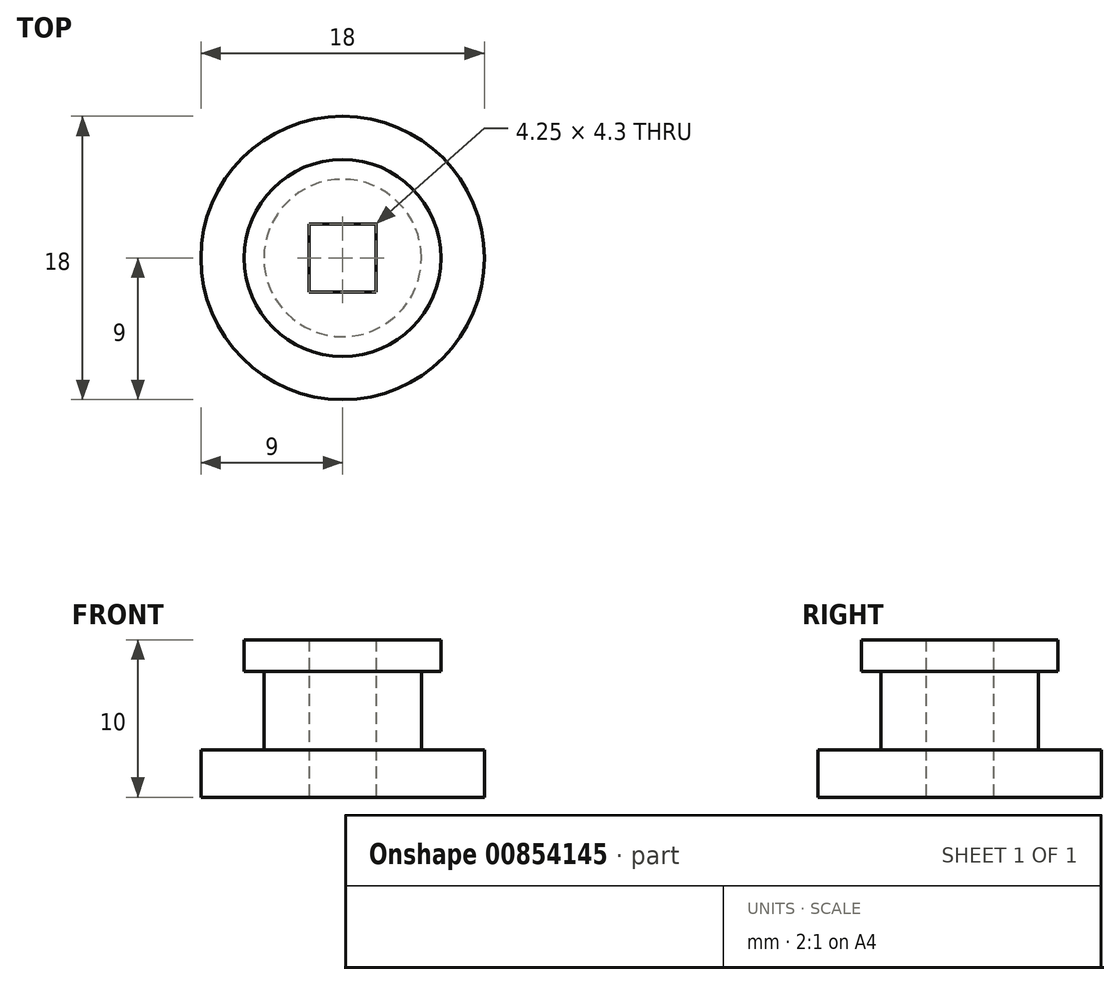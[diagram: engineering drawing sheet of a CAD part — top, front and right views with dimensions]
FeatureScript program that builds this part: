
annotation { "Feature Type Name" : "Feature", "Feature Type Description" : "" }
export const myFeature = defineFeature(function(context is Context, id is Id, definition is map)
    precondition{}
    {
        {
            var Q0;
            Q0=qCreatedBy(makeId("Top.planeOp"),FACE);
            var sketch = newSketch(context, id + "F0", { "sketchPlane" : qUnion([Q0])});
            skCircle(sketch, "E0", {"center": v(0, 0) * mm, "radius": 9 * mm});
            skCircle(sketch, "E1", {"center": v(0, 0) * mm, "radius": 5 * mm});
            skLineSegment(sketch, "E2.bottom", {"start": v(2.12, -2.15) * mm, "end": v(-2.12, -2.15) * mm});
            skLineSegment(sketch, "E2.top", {"start": v(2.12, 2.15) * mm, "end": v(-2.12, 2.15) * mm});
            skLineSegment(sketch, "E2.left", {"start": v(2.12, -2.15) * mm, "end": v(2.12, 2.15) * mm});
            skLineSegment(sketch, "E2.right", {"start": v(-2.12, -2.15) * mm, "end": v(-2.12, 2.15) * mm});
            skPoint(sketch, "E3.endSnap0", {"position": v(0, -2.15) * mm});
            skLineSegment(sketch, "E4.bottom", {"start": v(1, -7) * mm, "end": v(-1, -7) * mm, "construction": true});
            skLineSegment(sketch, "E4.top", {"start": v(1, -11) * mm, "end": v(-1, -11) * mm, "construction": true});
            skLineSegment(sketch, "E4.left", {"start": v(1, -7) * mm, "end": v(1, -11) * mm, "construction": true});
            skLineSegment(sketch, "E4.right", {"start": v(-1, -7) * mm, "end": v(-1, -11) * mm, "construction": true});
            skPoint(sketch, "E4.middle", {"position": v(0, -9) * mm});
            skLineSegment(sketch, "E5", {"start": v(-1, -8.94) * mm, "end": v(0, -11) * mm});
            skLineSegment(sketch, "E6", {"start": v(0, -11) * mm, "end": v(1, -8.94) * mm});
            skSolve(sketch);
        }
        {
            var Q0;
            Q0=makeQuery(id+"F0.imprint","IMPRINT",FACE,{"disambiguationData":[TD([[makeQuery(id+"F0.imprint","IMPRINT",EDGE,{"derivedFrom":sQuery(id+"F0.wireOp",EDGE,"E0")}),1.0]])]});
            extrude(context, id + "F1", {"entities" : qUnion([Q0]), "depth" : 3 * mm, "offsetDistance" : 25 * mm});
        }
        {
            var Q0;
            Q0=makeQuery(id+"F0.imprint","IMPRINT",FACE,{"disambiguationData":[TD([[makeQuery(id+"F0.imprint","IMPRINT",EDGE,{"derivedFrom":sQuery(id+"F0.wireOp",EDGE,"E1")}),1.0]])]});
            extrude(context, id + "F2", {"entities" : qUnion([Q0]), "operationType" : NewBodyOperationType.ADD, "depth" : 10 * mm, "offsetDistance" : 25 * mm});
        }
        {
            var Q0;
            Q0=makeQuery(id+"F2.opExtrude","CAP_FACE",FACE,{"disambiguationData":[OSD([sQuery(id+"F0.wireOp",EDGE,"E1"),sQuery(id+"F0.wireOp",EDGE,"E2.bottom"),sQuery(id+"F0.wireOp",EDGE,"E2.top"),sQuery(id+"F0.wireOp",EDGE,"E2.left"),sQuery(id+"F0.wireOp",EDGE,"E2.right")])],"isStart":false});
            var sketch = newSketch(context, id + "F3", { "sketchPlane" : qUnion([Q0])});
            skCircle(sketch, "E7", {"center": v(0, 0) * mm, "radius": 6.25 * mm});
            skSolve(sketch);
        }
        {
            var Q0;
            Q0=makeQuery(id+"F3.imprint","IMPRINT",FACE,{"disambiguationData":[TD([[makeQuery(id+"F3.imprint","IMPRINT",EDGE,{"derivedFrom":sQuery(id+"F3.wireOp",EDGE,"E7")}),1.0]])]});
            var Q1;
            Q1=makeQuery(id+"F3.imprint","IMPRINT",FACE,{"disambiguationData":[TD([[makeQuery(id+"F3.imprint","IMPRINT",EDGE,{"derivedFrom":makeQuery(id+"F2.opExtrude","CAP_EDGE",EDGE,{"disambiguationData":[OSD([sQuery(id+"F0.wireOp",EDGE,"E1")])],"isStart":false})}),1.0]])]});
            extrude(context, id + "F4", {"entities" : qUnion([Q0, Q1]), "operationType" : NewBodyOperationType.ADD, "oppositeDirection" : true, "depth" : 2 * mm, "offsetDistance" : 25 * mm});
        }
    });
